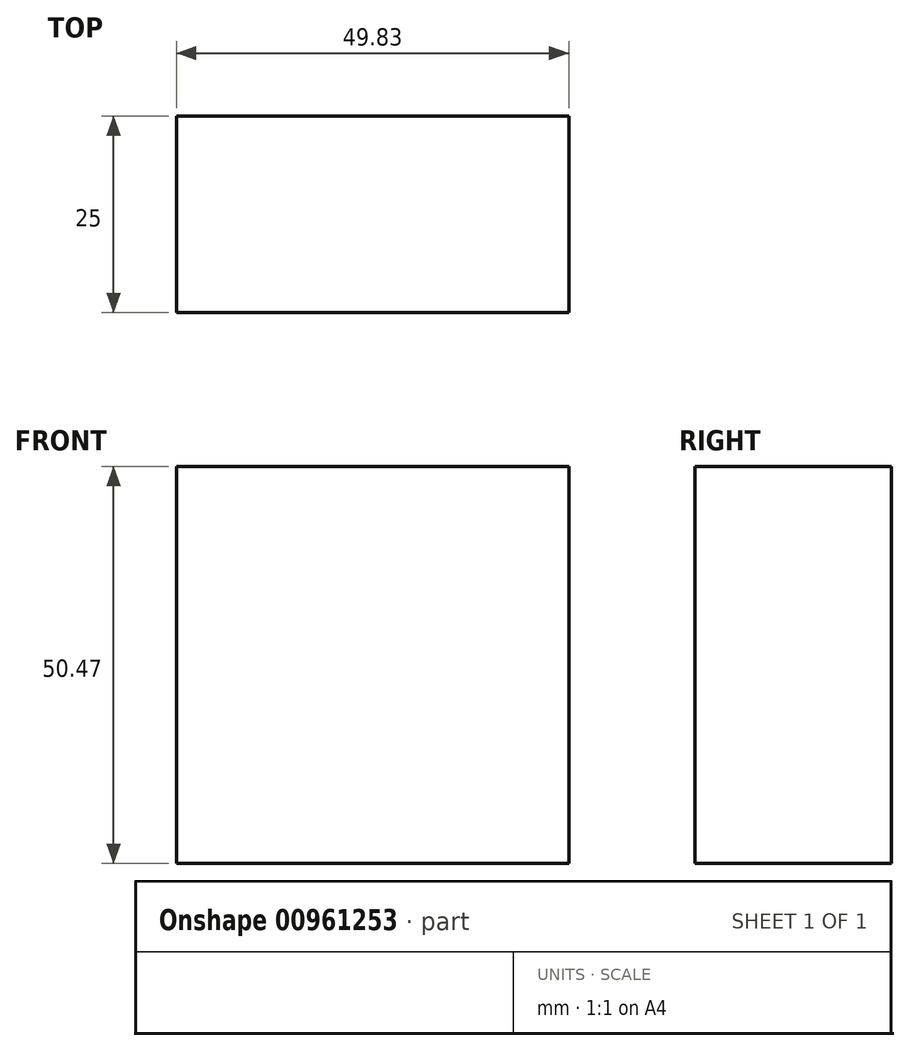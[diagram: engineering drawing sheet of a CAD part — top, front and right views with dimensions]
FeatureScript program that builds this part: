
annotation { "Feature Type Name" : "Feature", "Feature Type Description" : "" }
export const myFeature = defineFeature(function(context is Context, id is Id, definition is map)
    precondition{}
    {
        {
            var Q0;
            Q0=qCreatedBy(makeId("Front.planeOp"),FACE);
            var sketch = newSketch(context, id + "F0", { "sketchPlane" : qUnion([Q0])});
            skLineSegment(sketch, "E0.bottom", {"start": v(0, 0) * mm, "end": v(49.83, 0) * mm});
            skLineSegment(sketch, "E0.top", {"start": v(0, 50.47) * mm, "end": v(49.83, 50.47) * mm});
            skLineSegment(sketch, "E0.left", {"start": v(0, 0) * mm, "end": v(0, 50.47) * mm});
            skLineSegment(sketch, "E0.right", {"start": v(49.83, 0) * mm, "end": v(49.83, 50.47) * mm});
            skSolve(sketch);
        }
        {
            var Q0;
            Q0=makeQuery(id+"F0.imprint","IMPRINT",FACE,{"disambiguationData":[TD([[makeQuery(id+"F0.imprint","IMPRINT",EDGE,{"derivedFrom":sQuery(id+"F0.wireOp",EDGE,"E0.bottom")}),1.0]])]});
            extrude(context, id + "F1", {"entities" : qUnion([Q0]), "depth" : 25 * mm, "offsetDistance" : 25 * mm});
        }
    });
